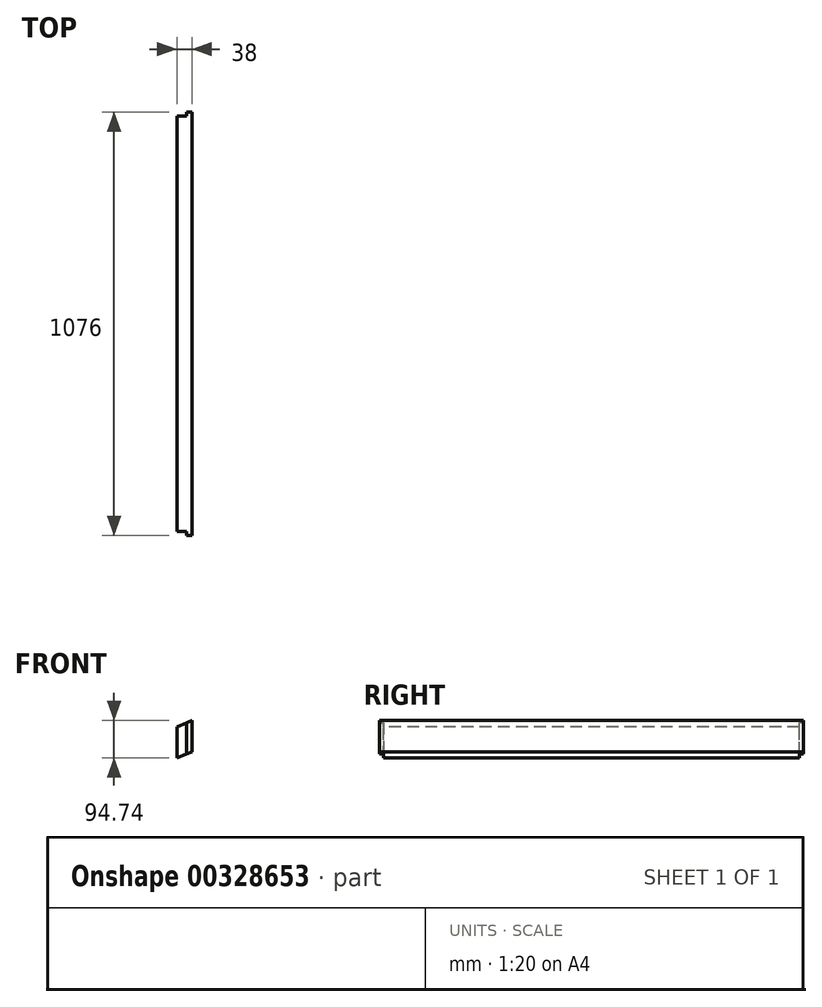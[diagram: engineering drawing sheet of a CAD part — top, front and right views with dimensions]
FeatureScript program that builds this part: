
annotation { "Feature Type Name" : "Feature", "Feature Type Description" : "" }
export const myFeature = defineFeature(function(context is Context, id is Id, definition is map)
    precondition{}
    {
        {
            var Q0;
            Q0=qCreatedBy(makeId("Front.planeOp"),FACE);
            var sketch = newSketch(context, id + "F0", { "sketchPlane" : qUnion([Q0])});
            skLineSegment(sketch, "E0", {"start": v(0, 0) * mm, "end": v(0, 79) * mm});
            skLineSegment(sketch, "E1", {"start": v(0, 79) * mm, "end": v(38, 94.74) * mm});
            skLineSegment(sketch, "E2", {"start": v(38, 94.74) * mm, "end": v(38, 15.74) * mm});
            skLineSegment(sketch, "E3", {"start": v(38, 15.74) * mm, "end": v(0, 0) * mm});
            skSolve(sketch);
        }
        {
            var Q0;
            Q0=qSketchRegion(id+"F0",true);
            extrude(context, id + "F1", {"entities" : qUnion([Q0]), "oppositeDirection" : true, "depth" : 1056 * mm});
        }
        {
            var Q0;
            Q0=makeQuery(id+"F1.opExtrude","CAP_FACE",FACE,{"disambiguationData":[OSD([sQuery(id+"F0.wireOp",EDGE,"E0"),sQuery(id+"F0.wireOp",EDGE,"E1"),sQuery(id+"F0.wireOp",EDGE,"E2"),sQuery(id+"F0.wireOp",EDGE,"E3")])],"isStart":true});
            var sketch = newSketch(context, id + "F2", { "sketchPlane" : qUnion([Q0])});
            skLineSegment(sketch, "E4", {"start": v(25, 89.36) * mm, "end": v(25, 10.36) * mm});
            skLineSegment(sketch, "E5", {"start": v(25, 10.36) * mm, "end": v(38, 15.74) * mm});
            skLineSegment(sketch, "E6", {"start": v(38, 15.74) * mm, "end": v(38, 94.74) * mm});
            skLineSegment(sketch, "E7", {"start": v(38, 94.74) * mm, "end": v(25, 89.36) * mm});
            skSolve(sketch);
        }
        {
            var Q0;
            Q0=qSketchRegion(id+"F2",true);
            extrude(context, id + "F3", {"entities" : qUnion([Q0]), "operationType" : NewBodyOperationType.ADD, "depth" : 10 * mm});
        }
        {
            var Q0;
            Q0=makeQuery(id+"F1.opExtrude","CAP_FACE",FACE,{"disambiguationData":[OSD([sQuery(id+"F0.wireOp",EDGE,"E0"),sQuery(id+"F0.wireOp",EDGE,"E1"),sQuery(id+"F0.wireOp",EDGE,"E2"),sQuery(id+"F0.wireOp",EDGE,"E3")])],"isStart":false});
            var sketch = newSketch(context, id + "F4", { "sketchPlane" : qUnion([Q0])});
            skLineSegment(sketch, "E8", {"start": v(-38, 15.74) * mm, "end": v(-25, 10.36) * mm});
            skLineSegment(sketch, "E9", {"start": v(-25, 10.36) * mm, "end": v(-25, 89.36) * mm});
            skLineSegment(sketch, "E10", {"start": v(-25, 89.36) * mm, "end": v(-38, 94.74) * mm});
            skLineSegment(sketch, "E11", {"start": v(-38, 94.74) * mm, "end": v(-38, 15.74) * mm});
            skSolve(sketch);
        }
        {
            var Q0;
            Q0=qSketchRegion(id+"F4",true);
            extrude(context, id + "F5", {"entities" : qUnion([Q0]), "operationType" : NewBodyOperationType.ADD, "depth" : 10 * mm});
        }
    });
